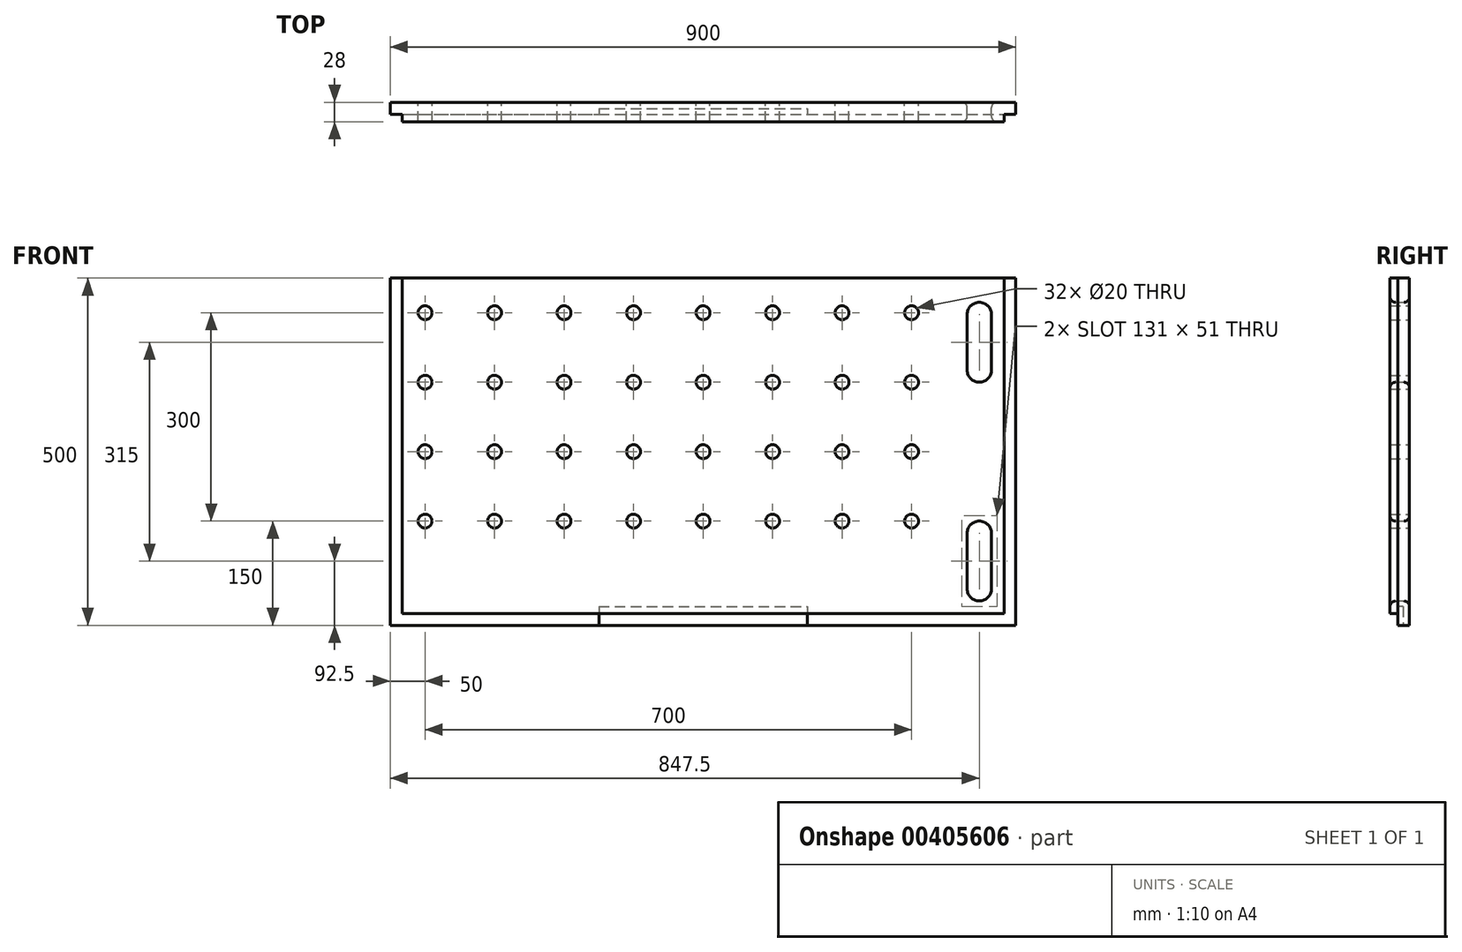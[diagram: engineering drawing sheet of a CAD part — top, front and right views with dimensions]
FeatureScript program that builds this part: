
annotation { "Feature Type Name" : "Feature", "Feature Type Description" : "" }
export const myFeature = defineFeature(function(context is Context, id is Id, definition is map)
    precondition{}
    {
        {
            var Q0;
            Q0=qCreatedBy(makeId("Front.planeOp"),FACE);
            var sketch = newSketch(context, id + "F0", { "sketchPlane" : qUnion([Q0])});
            skLineSegment(sketch, "E0.bottom", {"start": v(-450, -250) * mm, "end": v(450, -250) * mm});
            skLineSegment(sketch, "E0.top", {"start": v(-450, 250) * mm, "end": v(450, 250) * mm});
            skLineSegment(sketch, "E0.left", {"start": v(-450, -250) * mm, "end": v(-450, 250) * mm});
            skLineSegment(sketch, "E0.right", {"start": v(450, -250) * mm, "end": v(450, 250) * mm});
            skSolve(sketch);
        }
        {
            var Q0;
            Q0 = qSketchRegion(id + "F0", true);
            extrude(context, id + "F1", {"entities" : qUnion([Q0]), "depth" : 28 * mm});
        }
        {
            var Q0;
            Q0=makeQuery(id+"F1.opExtrude","CAP_FACE",FACE,{"disambiguationData":[OSD([sQuery(id+"F0.wireOp",EDGE,"E0.bottom"),sQuery(id+"F0.wireOp",EDGE,"E0.top"),sQuery(id+"F0.wireOp",EDGE,"E0.left"),sQuery(id+"F0.wireOp",EDGE,"E0.right")])],"isStart":false});
            var sketch = newSketch(context, id + "F2", { "sketchPlane" : qUnion([Q0])});
            skCircle(sketch, "E1", {"center": v(300, -100) * mm, "radius": 10 * mm});
            skCircle(sketch, "E2", {"center": v(200, -100) * mm, "radius": 10 * mm});
            skCircle(sketch, "E3", {"center": v(100, -100) * mm, "radius": 10 * mm});
            skCircle(sketch, "E4", {"center": v(0, -100) * mm, "radius": 10 * mm});
            skCircle(sketch, "E5", {"center": v(-100, -100) * mm, "radius": 10 * mm});
            skCircle(sketch, "E6", {"center": v(-200, -100) * mm, "radius": 10 * mm});
            skCircle(sketch, "E7", {"center": v(-300, -100) * mm, "radius": 10 * mm});
            skCircle(sketch, "E8", {"center": v(-400, -100) * mm, "radius": 10 * mm});
            skLineSegment(sketch, "E9", {"start": v(-450, -50) * mm, "end": v(450, -50) * mm, "construction": true});
            skCircle(sketch, "E10.MirrorC", {"center": v(-400, 0) * mm, "radius": 10 * mm});
            skCircle(sketch, "E11.MirrorC", {"center": v(-300, 0) * mm, "radius": 10 * mm});
            skCircle(sketch, "E12.MirrorC", {"center": v(-200, 0) * mm, "radius": 10 * mm});
            skCircle(sketch, "E13.MirrorC", {"center": v(-100, 0) * mm, "radius": 10 * mm});
            skCircle(sketch, "E14.MirrorC", {"center": v(0, 0) * mm, "radius": 10 * mm});
            skCircle(sketch, "E15.MirrorC", {"center": v(100, 0) * mm, "radius": 10 * mm});
            skCircle(sketch, "E16.MirrorC", {"center": v(200, 0) * mm, "radius": 10 * mm});
            skCircle(sketch, "E17.MirrorC", {"center": v(300, 0) * mm, "radius": 10 * mm});
            skLineSegment(sketch, "E18", {"start": v(-450, 50) * mm, "end": v(450, 50) * mm, "construction": true});
            skCircle(sketch, "E19.MirrorC", {"center": v(-400, 100) * mm, "radius": 10 * mm});
            skCircle(sketch, "E20.MirrorC", {"center": v(-300, 100) * mm, "radius": 10 * mm});
            skCircle(sketch, "E21.MirrorC", {"center": v(-200, 100) * mm, "radius": 10 * mm});
            skCircle(sketch, "E22.MirrorC", {"center": v(-100, 100) * mm, "radius": 10 * mm});
            skCircle(sketch, "E23.MirrorC", {"center": v(0, 100) * mm, "radius": 10 * mm});
            skCircle(sketch, "E24.MirrorC", {"center": v(100, 100) * mm, "radius": 10 * mm});
            skCircle(sketch, "E25.MirrorC", {"center": v(200, 100) * mm, "radius": 10 * mm});
            skCircle(sketch, "E26.MirrorC", {"center": v(300, 100) * mm, "radius": 10 * mm});
            skLineSegment(sketch, "E27", {"start": v(-450, 150) * mm, "end": v(450, 150) * mm, "construction": true});
            skCircle(sketch, "E28.MirrorC", {"center": v(-400, 200) * mm, "radius": 10 * mm});
            skCircle(sketch, "E29.MirrorC", {"center": v(-300, 200) * mm, "radius": 10 * mm});
            skCircle(sketch, "E30.MirrorC", {"center": v(-200, 200) * mm, "radius": 10 * mm});
            skCircle(sketch, "E31.MirrorC", {"center": v(-100, 200) * mm, "radius": 10 * mm});
            skCircle(sketch, "E32.MirrorC", {"center": v(0, 200) * mm, "radius": 10 * mm});
            skCircle(sketch, "E33.MirrorC", {"center": v(100, 200) * mm, "radius": 10 * mm});
            skCircle(sketch, "E34.MirrorC", {"center": v(200, 200) * mm, "radius": 10 * mm});
            skCircle(sketch, "E35.MirrorC", {"center": v(300, 200) * mm, "radius": 10 * mm});
            skSolve(sketch);
        }
        {
            var Q0;
            Q0 = qSketchRegion(id + "F2", true);
            extrude(context, id + "F3", {"entities" : qUnion([Q0]), "depth" : 25 * mm, "hasSecondDirection" : true, "secondDirectionOppositeDirection" : true, "secondDirectionDepth" : 35 * mm});
        }
        {
            var Q0;
            Q0 = qSketchRegion(id + "F2", true);
            extrude(context, id + "F4", {"entities" : qUnion([Q0]), "depth" : 25 * mm, "hasSecondDirection" : true, "secondDirectionOppositeDirection" : true, "secondDirectionDepth" : 35 * mm});
        }
        {
            var Q0;
            Q0=makeQuery(id+"F3.opExtrude","SWEPT_BODY",BODY,{"disambiguationData":[OSD([sQuery(id+"F2.wireOp",EDGE,"E1")])]});
            var Q1;
            Q1=makeQuery(id+"F3.opExtrude","SWEPT_BODY",BODY,{"disambiguationData":[OSD([sQuery(id+"F2.wireOp",EDGE,"E2")])]});
            var Q2;
            Q2=makeQuery(id+"F3.opExtrude","SWEPT_BODY",BODY,{"disambiguationData":[OSD([sQuery(id+"F2.wireOp",EDGE,"E3")])]});
            var Q3;
            Q3=makeQuery(id+"F3.opExtrude","SWEPT_BODY",BODY,{"disambiguationData":[OSD([sQuery(id+"F2.wireOp",EDGE,"E4")])]});
            var Q4;
            Q4=makeQuery(id+"F3.opExtrude","SWEPT_BODY",BODY,{"disambiguationData":[OSD([sQuery(id+"F2.wireOp",EDGE,"E5")])]});
            var Q5;
            Q5=makeQuery(id+"F3.opExtrude","SWEPT_BODY",BODY,{"disambiguationData":[OSD([sQuery(id+"F2.wireOp",EDGE,"E6")])]});
            var Q6;
            Q6=makeQuery(id+"F3.opExtrude","SWEPT_BODY",BODY,{"disambiguationData":[OSD([sQuery(id+"F2.wireOp",EDGE,"E7")])]});
            var Q7;
            Q7=makeQuery(id+"F3.opExtrude","SWEPT_BODY",BODY,{"disambiguationData":[OSD([sQuery(id+"F2.wireOp",EDGE,"E8")])]});
            var Q8;
            Q8=makeQuery(id+"F3.opExtrude","SWEPT_BODY",BODY,{"disambiguationData":[OSD([sQuery(id+"F2.wireOp",EDGE,"E10.MirrorC")])]});
            var Q9;
            Q9=makeQuery(id+"F3.opExtrude","SWEPT_BODY",BODY,{"disambiguationData":[OSD([sQuery(id+"F2.wireOp",EDGE,"E11.MirrorC")])]});
            var Q10;
            Q10=makeQuery(id+"F3.opExtrude","SWEPT_BODY",BODY,{"disambiguationData":[OSD([sQuery(id+"F2.wireOp",EDGE,"E12.MirrorC")])]});
            var Q11;
            Q11=makeQuery(id+"F3.opExtrude","SWEPT_BODY",BODY,{"disambiguationData":[OSD([sQuery(id+"F2.wireOp",EDGE,"E13.MirrorC")])]});
            var Q12;
            Q12=makeQuery(id+"F3.opExtrude","SWEPT_BODY",BODY,{"disambiguationData":[OSD([sQuery(id+"F2.wireOp",EDGE,"E14.MirrorC")])]});
            var Q13;
            Q13=makeQuery(id+"F3.opExtrude","SWEPT_BODY",BODY,{"disambiguationData":[OSD([sQuery(id+"F2.wireOp",EDGE,"E15.MirrorC")])]});
            var Q14;
            Q14=makeQuery(id+"F3.opExtrude","SWEPT_BODY",BODY,{"disambiguationData":[OSD([sQuery(id+"F2.wireOp",EDGE,"E16.MirrorC")])]});
            var Q15;
            Q15=makeQuery(id+"F3.opExtrude","SWEPT_BODY",BODY,{"disambiguationData":[OSD([sQuery(id+"F2.wireOp",EDGE,"E17.MirrorC")])]});
            var Q16;
            Q16=makeQuery(id+"F3.opExtrude","SWEPT_BODY",BODY,{"disambiguationData":[OSD([sQuery(id+"F2.wireOp",EDGE,"E19.MirrorC")])]});
            var Q17;
            Q17=makeQuery(id+"F3.opExtrude","SWEPT_BODY",BODY,{"disambiguationData":[OSD([sQuery(id+"F2.wireOp",EDGE,"E20.MirrorC")])]});
            var Q18;
            Q18=makeQuery(id+"F3.opExtrude","SWEPT_BODY",BODY,{"disambiguationData":[OSD([sQuery(id+"F2.wireOp",EDGE,"E21.MirrorC")])]});
            var Q19;
            Q19=makeQuery(id+"F3.opExtrude","SWEPT_BODY",BODY,{"disambiguationData":[OSD([sQuery(id+"F2.wireOp",EDGE,"E22.MirrorC")])]});
            var Q20;
            Q20=makeQuery(id+"F3.opExtrude","SWEPT_BODY",BODY,{"disambiguationData":[OSD([sQuery(id+"F2.wireOp",EDGE,"E23.MirrorC")])]});
            var Q21;
            Q21=makeQuery(id+"F3.opExtrude","SWEPT_BODY",BODY,{"disambiguationData":[OSD([sQuery(id+"F2.wireOp",EDGE,"E24.MirrorC")])]});
            var Q22;
            Q22=makeQuery(id+"F3.opExtrude","SWEPT_BODY",BODY,{"disambiguationData":[OSD([sQuery(id+"F2.wireOp",EDGE,"E25.MirrorC")])]});
            var Q23;
            Q23=makeQuery(id+"F3.opExtrude","SWEPT_BODY",BODY,{"disambiguationData":[OSD([sQuery(id+"F2.wireOp",EDGE,"E26.MirrorC")])]});
            var Q24;
            Q24=makeQuery(id+"F3.opExtrude","SWEPT_BODY",BODY,{"disambiguationData":[OSD([sQuery(id+"F2.wireOp",EDGE,"E28.MirrorC")])]});
            var Q25;
            Q25=makeQuery(id+"F3.opExtrude","SWEPT_BODY",BODY,{"disambiguationData":[OSD([sQuery(id+"F2.wireOp",EDGE,"E29.MirrorC")])]});
            var Q26;
            Q26=makeQuery(id+"F3.opExtrude","SWEPT_BODY",BODY,{"disambiguationData":[OSD([sQuery(id+"F2.wireOp",EDGE,"E30.MirrorC")])]});
            var Q27;
            Q27=makeQuery(id+"F3.opExtrude","SWEPT_BODY",BODY,{"disambiguationData":[OSD([sQuery(id+"F2.wireOp",EDGE,"E31.MirrorC")])]});
            var Q28;
            Q28=makeQuery(id+"F3.opExtrude","SWEPT_BODY",BODY,{"disambiguationData":[OSD([sQuery(id+"F2.wireOp",EDGE,"E32.MirrorC")])]});
            var Q29;
            Q29=makeQuery(id+"F3.opExtrude","SWEPT_BODY",BODY,{"disambiguationData":[OSD([sQuery(id+"F2.wireOp",EDGE,"E33.MirrorC")])]});
            var Q30;
            Q30=makeQuery(id+"F3.opExtrude","SWEPT_BODY",BODY,{"disambiguationData":[OSD([sQuery(id+"F2.wireOp",EDGE,"E34.MirrorC")])]});
            var Q31;
            Q31=makeQuery(id+"F3.opExtrude","SWEPT_BODY",BODY,{"disambiguationData":[OSD([sQuery(id+"F2.wireOp",EDGE,"E35.MirrorC")])]});
            var Q32;
            Q32=makeQuery(id+"F4.opExtrude","SWEPT_BODY",BODY,{"disambiguationData":[OSD([sQuery(id+"F2.wireOp",EDGE,"E1")])]});
            var Q33;
            Q33=makeQuery(id+"F4.opExtrude","SWEPT_BODY",BODY,{"disambiguationData":[OSD([sQuery(id+"F2.wireOp",EDGE,"E2")])]});
            var Q34;
            Q34=makeQuery(id+"F4.opExtrude","SWEPT_BODY",BODY,{"disambiguationData":[OSD([sQuery(id+"F2.wireOp",EDGE,"E3")])]});
            var Q35;
            Q35=makeQuery(id+"F4.opExtrude","SWEPT_BODY",BODY,{"disambiguationData":[OSD([sQuery(id+"F2.wireOp",EDGE,"E4")])]});
            var Q36;
            Q36=makeQuery(id+"F4.opExtrude","SWEPT_BODY",BODY,{"disambiguationData":[OSD([sQuery(id+"F2.wireOp",EDGE,"E5")])]});
            var Q37;
            Q37=makeQuery(id+"F4.opExtrude","SWEPT_BODY",BODY,{"disambiguationData":[OSD([sQuery(id+"F2.wireOp",EDGE,"E6")])]});
            var Q38;
            Q38=makeQuery(id+"F4.opExtrude","SWEPT_BODY",BODY,{"disambiguationData":[OSD([sQuery(id+"F2.wireOp",EDGE,"E7")])]});
            var Q39;
            Q39=makeQuery(id+"F4.opExtrude","SWEPT_BODY",BODY,{"disambiguationData":[OSD([sQuery(id+"F2.wireOp",EDGE,"E8")])]});
            var Q40;
            Q40=makeQuery(id+"F4.opExtrude","SWEPT_BODY",BODY,{"disambiguationData":[OSD([sQuery(id+"F2.wireOp",EDGE,"E10.MirrorC")])]});
            var Q41;
            Q41=makeQuery(id+"F4.opExtrude","SWEPT_BODY",BODY,{"disambiguationData":[OSD([sQuery(id+"F2.wireOp",EDGE,"E11.MirrorC")])]});
            var Q42;
            Q42=makeQuery(id+"F4.opExtrude","SWEPT_BODY",BODY,{"disambiguationData":[OSD([sQuery(id+"F2.wireOp",EDGE,"E12.MirrorC")])]});
            var Q43;
            Q43=makeQuery(id+"F4.opExtrude","SWEPT_BODY",BODY,{"disambiguationData":[OSD([sQuery(id+"F2.wireOp",EDGE,"E13.MirrorC")])]});
            var Q44;
            Q44=makeQuery(id+"F4.opExtrude","SWEPT_BODY",BODY,{"disambiguationData":[OSD([sQuery(id+"F2.wireOp",EDGE,"E14.MirrorC")])]});
            var Q45;
            Q45=makeQuery(id+"F4.opExtrude","SWEPT_BODY",BODY,{"disambiguationData":[OSD([sQuery(id+"F2.wireOp",EDGE,"E15.MirrorC")])]});
            var Q46;
            Q46=makeQuery(id+"F4.opExtrude","SWEPT_BODY",BODY,{"disambiguationData":[OSD([sQuery(id+"F2.wireOp",EDGE,"E16.MirrorC")])]});
            var Q47;
            Q47=makeQuery(id+"F4.opExtrude","SWEPT_BODY",BODY,{"disambiguationData":[OSD([sQuery(id+"F2.wireOp",EDGE,"E17.MirrorC")])]});
            var Q48;
            Q48=makeQuery(id+"F4.opExtrude","SWEPT_BODY",BODY,{"disambiguationData":[OSD([sQuery(id+"F2.wireOp",EDGE,"E19.MirrorC")])]});
            var Q49;
            Q49=makeQuery(id+"F4.opExtrude","SWEPT_BODY",BODY,{"disambiguationData":[OSD([sQuery(id+"F2.wireOp",EDGE,"E20.MirrorC")])]});
            var Q50;
            Q50=makeQuery(id+"F4.opExtrude","SWEPT_BODY",BODY,{"disambiguationData":[OSD([sQuery(id+"F2.wireOp",EDGE,"E21.MirrorC")])]});
            var Q51;
            Q51=makeQuery(id+"F4.opExtrude","SWEPT_BODY",BODY,{"disambiguationData":[OSD([sQuery(id+"F2.wireOp",EDGE,"E22.MirrorC")])]});
            var Q52;
            Q52=makeQuery(id+"F4.opExtrude","SWEPT_BODY",BODY,{"disambiguationData":[OSD([sQuery(id+"F2.wireOp",EDGE,"E23.MirrorC")])]});
            var Q53;
            Q53=makeQuery(id+"F4.opExtrude","SWEPT_BODY",BODY,{"disambiguationData":[OSD([sQuery(id+"F2.wireOp",EDGE,"E24.MirrorC")])]});
            var Q54;
            Q54=makeQuery(id+"F4.opExtrude","SWEPT_BODY",BODY,{"disambiguationData":[OSD([sQuery(id+"F2.wireOp",EDGE,"E25.MirrorC")])]});
            var Q55;
            Q55=makeQuery(id+"F4.opExtrude","SWEPT_BODY",BODY,{"disambiguationData":[OSD([sQuery(id+"F2.wireOp",EDGE,"E26.MirrorC")])]});
            var Q56;
            Q56=makeQuery(id+"F4.opExtrude","SWEPT_BODY",BODY,{"disambiguationData":[OSD([sQuery(id+"F2.wireOp",EDGE,"E28.MirrorC")])]});
            var Q57;
            Q57=makeQuery(id+"F4.opExtrude","SWEPT_BODY",BODY,{"disambiguationData":[OSD([sQuery(id+"F2.wireOp",EDGE,"E29.MirrorC")])]});
            var Q58;
            Q58=makeQuery(id+"F4.opExtrude","SWEPT_BODY",BODY,{"disambiguationData":[OSD([sQuery(id+"F2.wireOp",EDGE,"E30.MirrorC")])]});
            var Q59;
            Q59=makeQuery(id+"F4.opExtrude","SWEPT_BODY",BODY,{"disambiguationData":[OSD([sQuery(id+"F2.wireOp",EDGE,"E31.MirrorC")])]});
            var Q60;
            Q60=makeQuery(id+"F4.opExtrude","SWEPT_BODY",BODY,{"disambiguationData":[OSD([sQuery(id+"F2.wireOp",EDGE,"E32.MirrorC")])]});
            var Q61;
            Q61=makeQuery(id+"F4.opExtrude","SWEPT_BODY",BODY,{"disambiguationData":[OSD([sQuery(id+"F2.wireOp",EDGE,"E33.MirrorC")])]});
            var Q62;
            Q62=makeQuery(id+"F4.opExtrude","SWEPT_BODY",BODY,{"disambiguationData":[OSD([sQuery(id+"F2.wireOp",EDGE,"E34.MirrorC")])]});
            var Q63;
            Q63=makeQuery(id+"F4.opExtrude","SWEPT_BODY",BODY,{"disambiguationData":[OSD([sQuery(id+"F2.wireOp",EDGE,"E35.MirrorC")])]});
            var Q64;
            Q64=makeQuery(id+"F1.opExtrude","SWEPT_BODY",BODY,{"disambiguationData":[OSD([sQuery(id+"F0.wireOp",EDGE,"E0.bottom"),sQuery(id+"F0.wireOp",EDGE,"E0.top"),sQuery(id+"F0.wireOp",EDGE,"E0.left"),sQuery(id+"F0.wireOp",EDGE,"E0.right")])]});
            booleanBodies(context, id + "F5", {"operationType" : BooleanOperationType.SUBTRACTION, "tools" : qUnion([Q0, Q1, Q2, Q3, Q4, Q5, Q6, Q7, Q8, Q9, Q10, Q11, Q12, Q13, Q14, Q15, Q16, Q17, Q18, Q19, Q20, Q21, Q22, Q23, Q24, Q25, Q26, Q27, Q28, Q29, Q30, Q31, Q32, Q33, Q34, Q35, Q36, Q37, Q38, Q39, Q40, Q41, Q42, Q43, Q44, Q45, Q46, Q47, Q48, Q49, Q50, Q51, Q52, Q53, Q54, Q55, Q56, Q57, Q58, Q59, Q60, Q61, Q62, Q63]), "targets" : qUnion([Q64])});
        }
        {
            var Q0;
            Q0=makeQuery(id+"F1.opExtrude","CAP_FACE",FACE,{"disambiguationData":[OSD([sQuery(id+"F0.wireOp",EDGE,"E0.bottom"),sQuery(id+"F0.wireOp",EDGE,"E0.top"),sQuery(id+"F0.wireOp",EDGE,"E0.left"),sQuery(id+"F0.wireOp",EDGE,"E0.right")])],"isStart":false});
            var sketch = newSketch(context, id + "F6", { "sketchPlane" : qUnion([Q0])});
            skLineSegment(sketch, "E36.bottom", {"start": v(450, 250) * mm, "end": v(433, 250) * mm});
            skLineSegment(sketch, "E36.top", {"start": v(450, -250) * mm, "end": v(433, -250) * mm});
            skLineSegment(sketch, "E36.left", {"start": v(450, 250) * mm, "end": v(450, -250) * mm});
            skLineSegment(sketch, "E36.right", {"start": v(433, 250) * mm, "end": v(433, -250) * mm});
            skLineSegment(sketch, "E37", {"start": v(0, 250) * mm, "end": v(0, -250) * mm, "construction": true});
            skLineSegment(sketch, "E38.MirrorCS", {"start": v(-433, 250) * mm, "end": v(-433, -250) * mm});
            skLineSegment(sketch, "E39.MirrorCS", {"start": v(-450, 250) * mm, "end": v(-433, 250) * mm});
            skLineSegment(sketch, "E40.MirrorCS", {"start": v(-450, 250) * mm, "end": v(-450, -250) * mm});
            skLineSegment(sketch, "E41.MirrorCS", {"start": v(-450, -250) * mm, "end": v(-433, -250) * mm});
            skSolve(sketch);
        }
        {
            var Q0;
            Q0 = qSketchRegion(id + "F6", true);
            extrude(context, id + "F7", {"entities" : qUnion([Q0]), "operationType" : NewBodyOperationType.REMOVE, "oppositeDirection" : true, "depth" : 11 * mm});
        }
        {
            var Q0;
            Q0=makeQuery(id+"F1.opExtrude","CAP_FACE",FACE,{"disambiguationData":[OSD([sQuery(id+"F0.wireOp",EDGE,"E0.bottom"),sQuery(id+"F0.wireOp",EDGE,"E0.top"),sQuery(id+"F0.wireOp",EDGE,"E0.left"),sQuery(id+"F0.wireOp",EDGE,"E0.right")])],"isStart":false});
            var sketch = newSketch(context, id + "F8", { "sketchPlane" : qUnion([Q0])});
            skLineSegment(sketch, "E42.left", {"start": v(415, -117.5) * mm, "end": v(415, -197.5) * mm});
            skLineSegment(sketch, "E42.right", {"start": v(380, -117.5) * mm, "end": v(380, -197.5) * mm});
            skArc(sketch, "E43", {"start": v(415, -117.5) * mm, "mid": v(397.5, -100) * mm, "end": v(380, -117.5) * mm});
            skArc(sketch, "E44", {"start": v(380, -197.5) * mm, "mid": v(397.5, -215) * mm, "end": v(415, -197.5) * mm});
            skLineSegment(sketch, "E45.left", {"start": v(415, 197.5) * mm, "end": v(415, 117.5) * mm});
            skLineSegment(sketch, "E45.right", {"start": v(380, 197.5) * mm, "end": v(380, 117.5) * mm});
            skArc(sketch, "E46", {"start": v(415, 197.5) * mm, "mid": v(397.5, 215) * mm, "end": v(380, 197.5) * mm});
            skArc(sketch, "E47", {"start": v(380, 117.5) * mm, "mid": v(397.5, 100) * mm, "end": v(415, 117.5) * mm});
            skSolve(sketch);
        }
        {
            var Q0;
            Q0 = qSketchRegion(id + "F8", true);
            extrude(context, id + "F9", {"entities" : qUnion([Q0]), "operationType" : NewBodyOperationType.REMOVE, "depth" : 25 * mm, "hasSecondDirection" : true, "secondDirectionOppositeDirection" : true, "secondDirectionDepth" : 35 * mm});
        }
        {
            var Q0;
            Q0=makeQuery(id+"F9.boolean.opBoolean","INTERSECT",EDGE,{"derivedFrom":[makeQuery(id+"F1.opExtrude","CAP_FACE",FACE,{"disambiguationData":[OSD([sQuery(id+"F0.wireOp",EDGE,"E0.bottom"),sQuery(id+"F0.wireOp",EDGE,"E0.top"),sQuery(id+"F0.wireOp",EDGE,"E0.left"),sQuery(id+"F0.wireOp",EDGE,"E0.right")])],"isStart":false}),makeQuery(id+"F9.opExtrude","SWEPT_FACE",FACE,{"disambiguationData":[OSD([sQuery(id+"F8.wireOp",EDGE,"E47")])]})]});
            var Q1;
            Q1=makeQuery(id+"F9.boolean.opBoolean","INTERSECT",EDGE,{"derivedFrom":[makeQuery(id+"F1.opExtrude","CAP_FACE",FACE,{"disambiguationData":[OSD([sQuery(id+"F0.wireOp",EDGE,"E0.bottom"),sQuery(id+"F0.wireOp",EDGE,"E0.top"),sQuery(id+"F0.wireOp",EDGE,"E0.left"),sQuery(id+"F0.wireOp",EDGE,"E0.right")])],"isStart":true}),makeQuery(id+"F9.opExtrude","SWEPT_FACE",FACE,{"disambiguationData":[OSD([sQuery(id+"F8.wireOp",EDGE,"E47")])]})]});
            var Q2;
            Q2=makeQuery(id+"F9.boolean.opBoolean","INTERSECT",EDGE,{"derivedFrom":[makeQuery(id+"F1.opExtrude","CAP_FACE",FACE,{"disambiguationData":[OSD([sQuery(id+"F0.wireOp",EDGE,"E0.bottom"),sQuery(id+"F0.wireOp",EDGE,"E0.top"),sQuery(id+"F0.wireOp",EDGE,"E0.left"),sQuery(id+"F0.wireOp",EDGE,"E0.right")])],"isStart":false}),makeQuery(id+"F9.opExtrude","SWEPT_FACE",FACE,{"disambiguationData":[OSD([sQuery(id+"F8.wireOp",EDGE,"E44")])]})]});
            var Q3;
            Q3=makeQuery(id+"F9.boolean.opBoolean","INTERSECT",EDGE,{"derivedFrom":[makeQuery(id+"F1.opExtrude","CAP_FACE",FACE,{"disambiguationData":[OSD([sQuery(id+"F0.wireOp",EDGE,"E0.bottom"),sQuery(id+"F0.wireOp",EDGE,"E0.top"),sQuery(id+"F0.wireOp",EDGE,"E0.left"),sQuery(id+"F0.wireOp",EDGE,"E0.right")])],"isStart":true}),makeQuery(id+"F9.opExtrude","SWEPT_FACE",FACE,{"disambiguationData":[OSD([sQuery(id+"F8.wireOp",EDGE,"E44")])]})]});
            fillet(context, id + "F10", {"entities" : qUnion([Q0, Q1, Q2, Q3]), "radius" : 8 * mm, "tangentPropagation" : true, "allowEdgeOverflow" : false});
        }
        {
            var Q0;
            Q0=makeQuery(id+"F1.opExtrude","CAP_FACE",FACE,{"disambiguationData":[OSD([sQuery(id+"F0.wireOp",EDGE,"E0.bottom"),sQuery(id+"F0.wireOp",EDGE,"E0.top"),sQuery(id+"F0.wireOp",EDGE,"E0.left"),sQuery(id+"F0.wireOp",EDGE,"E0.right")])],"isStart":false});
            var sketch = newSketch(context, id + "F11", { "sketchPlane" : qUnion([Q0])});
            skLineSegment(sketch, "E48.bottom", {"start": v(-433, -250) * mm, "end": v(433, -250) * mm});
            skLineSegment(sketch, "E48.top", {"start": v(-433, -233) * mm, "end": v(433, -233) * mm});
            skLineSegment(sketch, "E48.left", {"start": v(-433, -250) * mm, "end": v(-433, -233) * mm});
            skLineSegment(sketch, "E48.right", {"start": v(433, -250) * mm, "end": v(433, -233) * mm});
            skSolve(sketch);
        }
        {
            var Q0;
            Q0 = qSketchRegion(id + "F11", true);
            extrude(context, id + "F12", {"entities" : qUnion([Q0]), "operationType" : NewBodyOperationType.REMOVE, "oppositeDirection" : true, "depth" : 11 * mm});
        }
        {
            var Q0;
            Q0=makeQuery(id+"F12.boolean.opBoolean","MERGE",FACE,{"derivedFrom":[makeQuery(id+"F7.boolean.opBoolean","COPY",FACE,{"derivedFrom":makeQuery(id+"F7.opExtrude","CAP_FACE",FACE,{"disambiguationData":[OSD([sQuery(id+"F6.wireOp",EDGE,"E36.bottom"),sQuery(id+"F6.wireOp",EDGE,"E36.top"),sQuery(id+"F6.wireOp",EDGE,"E36.left"),sQuery(id+"F6.wireOp",EDGE,"E36.right")])],"isStart":false})}),makeQuery(id+"F7.boolean.opBoolean","COPY",FACE,{"derivedFrom":makeQuery(id+"F7.opExtrude","CAP_FACE",FACE,{"disambiguationData":[OSD([sQuery(id+"F6.wireOp",EDGE,"E38.MirrorCS"),sQuery(id+"F6.wireOp",EDGE,"E39.MirrorCS"),sQuery(id+"F6.wireOp",EDGE,"E40.MirrorCS"),sQuery(id+"F6.wireOp",EDGE,"E41.MirrorCS")])],"isStart":false})}),makeQuery(id+"F12.opExtrude","CAP_FACE",FACE,{"disambiguationData":[OSD([sQuery(id+"F11.wireOp",EDGE,"E48.bottom"),sQuery(id+"F11.wireOp",EDGE,"E48.top"),sQuery(id+"F11.wireOp",EDGE,"E48.left"),sQuery(id+"F11.wireOp",EDGE,"E48.right")])],"isStart":false})]});
            var sketch = newSketch(context, id + "F13", { "sketchPlane" : qUnion([Q0])});
            skLineSegment(sketch, "E49.bottom", {"start": v(-150, -223) * mm, "end": v(150, -223) * mm});
            skLineSegment(sketch, "E49.top", {"start": v(-150, -250) * mm, "end": v(150, -250) * mm});
            skLineSegment(sketch, "E49.left", {"start": v(-150, -223) * mm, "end": v(-150, -250) * mm});
            skLineSegment(sketch, "E49.right", {"start": v(150, -223) * mm, "end": v(150, -250) * mm});
            skLineSegment(sketch, "E50", {"start": v(0, -233) * mm, "end": v(0, -250) * mm, "construction": true});
            skSolve(sketch);
        }
        {
            var Q0;
            Q0 = qSketchRegion(id + "F13", true);
            extrude(context, id + "F14", {"entities" : qUnion([Q0]), "operationType" : NewBodyOperationType.REMOVE, "oppositeDirection" : true, "depth" : 8 * mm});
        }
    });
